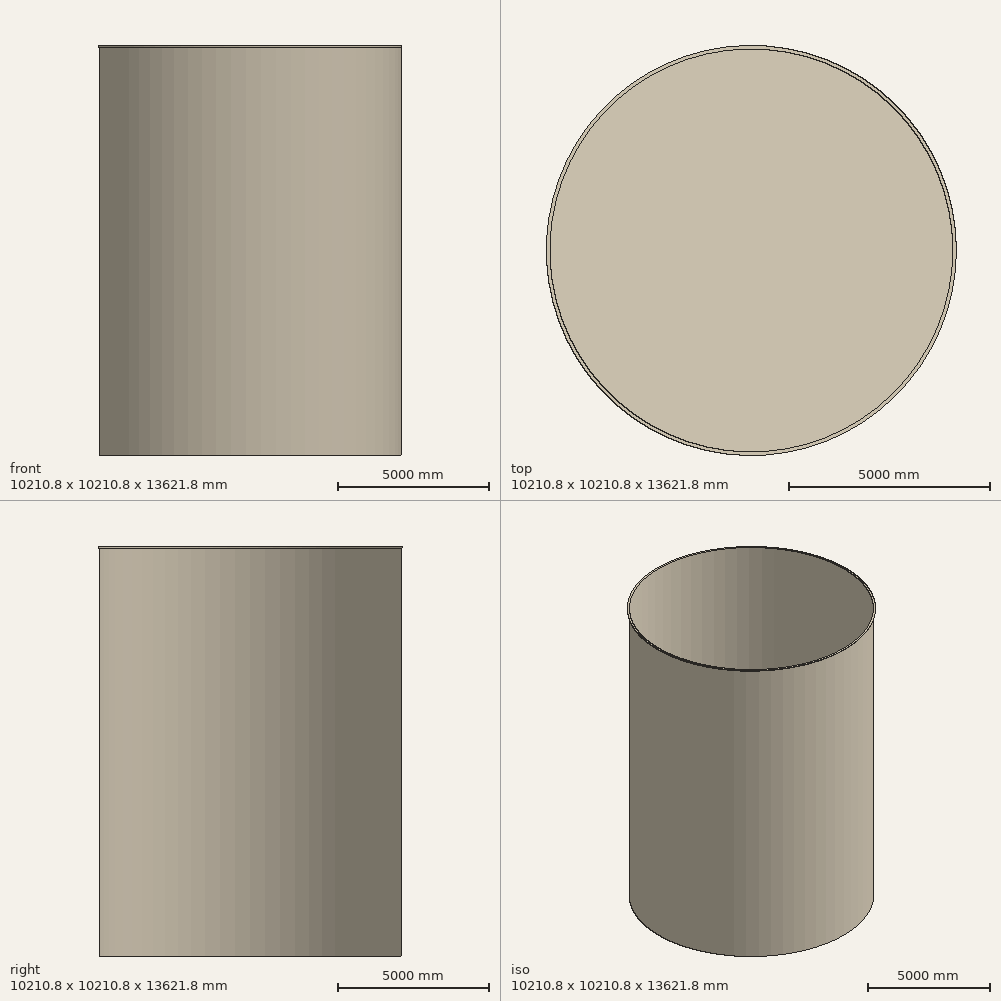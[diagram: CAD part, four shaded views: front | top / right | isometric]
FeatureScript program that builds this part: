
annotation { "Feature Type Name" : "Feature", "Feature Type Description" : "" }
export const myFeature = defineFeature(function(context is Context, id is Id, definition is map)
    precondition{}
    {
        {
            var Q0;
            Q0=qCreatedBy(makeId("Top.planeOp"),FACE);
            var sketch = newSketch(context, id + "F0", { "sketchPlane" : qUnion([Q0])});
            skCircle(sketch, "E0", {"center": v(0, 0) * mm, "radius": 5029.2 * mm});
            skCircle(sketch, "E1", {"center": v(0, 0) * mm, "radius": 5016.5 * mm});
            skSolve(sketch);
        }
        {
            var Q0;
            Q0=makeQuery(id+"F0.imprint","IMPRINT",FACE,{"disambiguationData":[TD([[makeQuery(id+"F0.imprint","IMPRINT",EDGE,{"derivedFrom":sQuery(id+"F0.wireOp",EDGE,"E0")}),1.0]])]});
            extrude(context, id + "F1", {"entities" : qUnion([Q0]), "depth" : 13615.42 * mm});
        }
        {
            var Q0;
            Q0=makeQuery(id+"F1.opExtrude","CAP_FACE",FACE,{"disambiguationData":[OSD([sQuery(id+"F0.wireOp",EDGE,"E0"),sQuery(id+"F0.wireOp",EDGE,"E1")])],"isStart":true});
            var sketch = newSketch(context, id + "F2", { "sketchPlane" : qUnion([Q0])});
            skCircle(sketch, "E2", {"center": v(0, 0) * mm, "radius": 5100 * mm});
            skSolve(sketch);
        }
        {
            var Q0;
            Q0=makeQuery(id+"F2.imprint","IMPRINT",FACE,{"disambiguationData":[TD([[makeQuery(id+"F2.imprint","IMPRINT",EDGE,{"derivedFrom":makeQuery(id+"F1.opExtrude","CAP_EDGE",EDGE,{"disambiguationData":[OSD([sQuery(id+"F0.wireOp",EDGE,"E1")])],"isStart":true})}),-1.0]])]});
            extrude(context, id + "F3", {"entities" : qUnion([Q0]), "depth" : 6.35 * mm});
        }
        {
            var Q0;
            Q0=makeQuery(id+"F1.opExtrude","CAP_FACE",FACE,{"disambiguationData":[OSD([sQuery(id+"F0.wireOp",EDGE,"E0"),sQuery(id+"F0.wireOp",EDGE,"E1")])],"isStart":false});
            var sketch = newSketch(context, id + "F4", { "sketchPlane" : qUnion([Q0])});
            skCircle(sketch, "E3", {"center": v(0, 0) * mm, "radius": 5105.4 * mm});
            skCircle(sketch, "E4", {"center": v(0, 0) * mm, "radius": 5029.2 * mm});
            skSolve(sketch);
        }
        {
            var Q0;
            Q0=makeQuery(id+"F4.imprint","IMPRINT",FACE,{"disambiguationData":[TD([[makeQuery(id+"F4.imprint","IMPRINT",EDGE,{"derivedFrom":sQuery(id+"F4.wireOp",EDGE,"E3")}),1.0]])]});
            extrude(context, id + "F5", {"entities" : qUnion([Q0]), "oppositeDirection" : true, "depth" : 12.7 * mm});
        }
        {
            var Q0;
            Q0=makeQuery(id+"F5.opExtrude","CAP_FACE",FACE,{"disambiguationData":[OSD([sQuery(id+"F4.wireOp",EDGE,"E3"),sQuery(id+"F4.wireOp",EDGE,"E4")])],"isStart":false});
            var sketch = newSketch(context, id + "F6", { "sketchPlane" : qUnion([Q0])});
            skCircle(sketch, "E5", {"center": v(0, 0) * mm, "radius": 5029.2 * mm});
            skCircle(sketch, "E6", {"center": v(0, 0) * mm, "radius": 5041.9 * mm});
            skSolve(sketch);
        }
        {
            var Q0;
            Q0=makeQuery(id+"F6.imprint","IMPRINT",FACE,{"disambiguationData":[TD([[makeQuery(id+"F6.imprint","IMPRINT",EDGE,{"derivedFrom":sQuery(id+"F6.wireOp",EDGE,"E5")}),1.0]])]});
            extrude(context, id + "F7", {"entities" : qUnion([Q0]), "depth" : 50.8 * mm});
        }
        {
            var Q0;
            Q0=makeQuery(id+"F1.opExtrude","SWEPT_BODY",BODY,{"disambiguationData":[OSD([sQuery(id+"F0.wireOp",EDGE,"E0"),sQuery(id+"F0.wireOp",EDGE,"E1")])]});
            var Q1;
            Q1=makeQuery(id+"F7.opExtrude","SWEPT_BODY",BODY,{"disambiguationData":[OSD([sQuery(id+"F6.wireOp",EDGE,"E5"),sQuery(id+"F6.wireOp",EDGE,"E6")])]});
            var Q2;
            Q2=makeQuery(id+"F3.opExtrude","SWEPT_BODY",BODY,{"disambiguationData":[OSD([sQuery(id+"F0.wireOp",EDGE,"E1")])]});
            var Q3;
            Q3=makeQuery(id+"F5.opExtrude","SWEPT_BODY",BODY,{"disambiguationData":[OSD([sQuery(id+"F4.wireOp",EDGE,"E3"),sQuery(id+"F4.wireOp",EDGE,"E4")])]});
            booleanBodies(context, id + "F8", {"operationType" : BooleanOperationType.UNION, "tools" : qUnion([Q0, Q1, Q2, Q3])});
        }
    });
